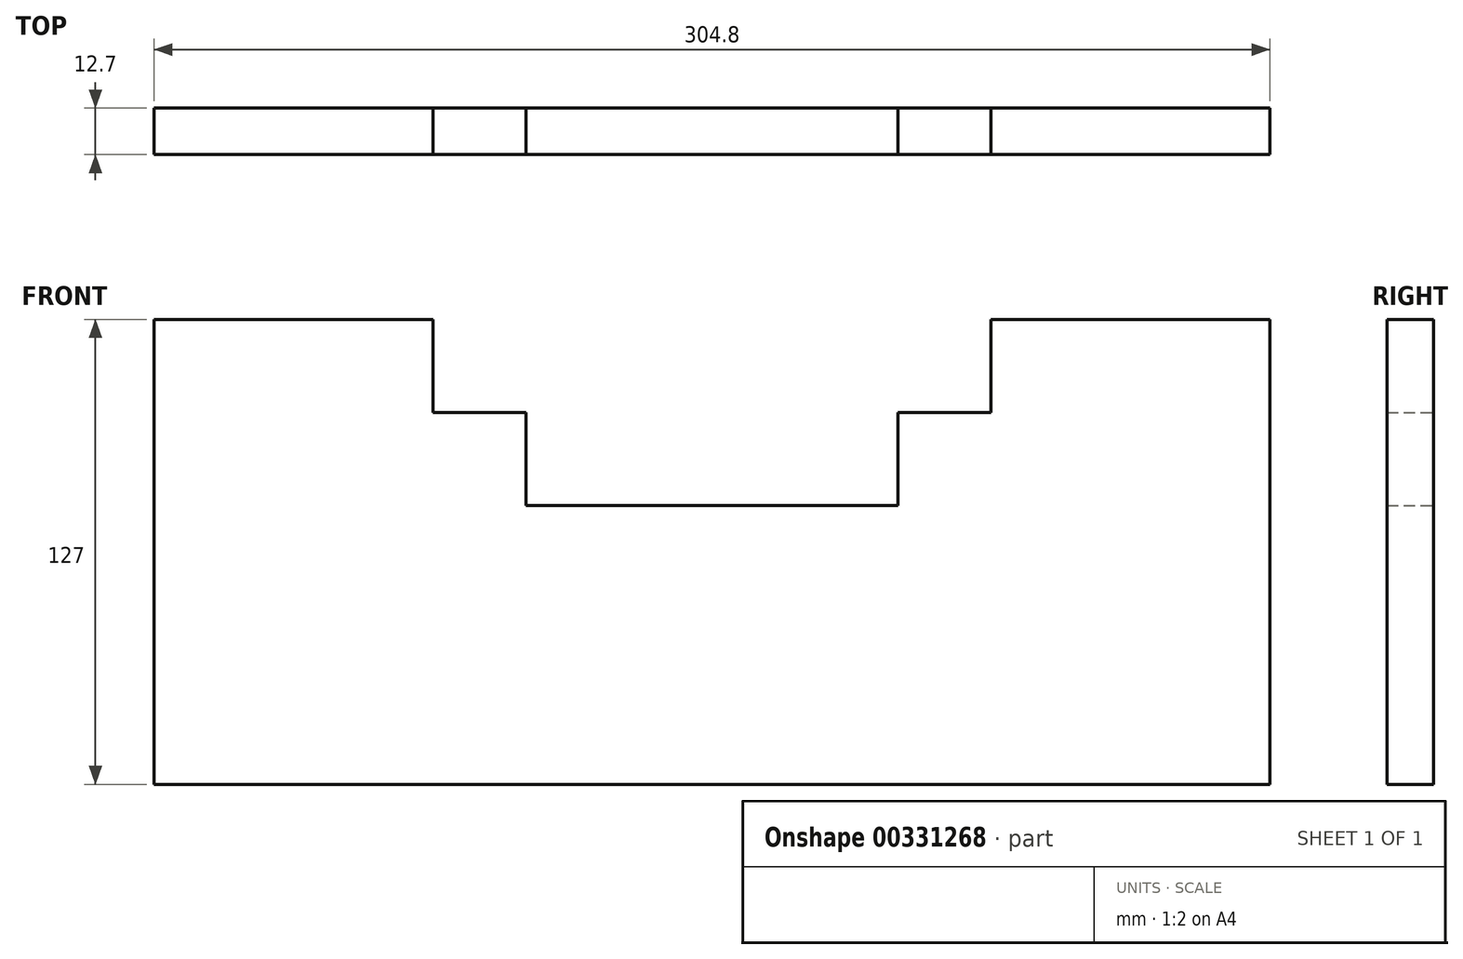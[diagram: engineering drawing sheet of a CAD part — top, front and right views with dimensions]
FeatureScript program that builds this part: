
annotation { "Feature Type Name" : "Feature", "Feature Type Description" : "" }
export const myFeature = defineFeature(function(context is Context, id is Id, definition is map)
    precondition{}
    {
        {
            var Q0;
            Q0=qCreatedBy(makeId("Front.planeOp"),FACE);
            var sketch = newSketch(context, id + "F0", { "sketchPlane" : qUnion([Q0])});
            skLineSegment(sketch, "E0.bottom", {"start": v(-50.8, 76.2) * mm, "end": v(50.8, 76.2) * mm});
            skLineSegment(sketch, "E0.top", {"start": v(-152.4, 0) * mm, "end": v(152.4, 0) * mm});
            skLineSegment(sketch, "E1.bottom", {"start": v(-76.2, 127) * mm, "end": v(-152.4, 127) * mm});
            skLineSegment(sketch, "E1.left", {"start": v(-76.2, 127) * mm, "end": v(-76.2, 101.6) * mm});
            skLineSegment(sketch, "E2.top", {"start": v(152.4, 127) * mm, "end": v(76.2, 127) * mm});
            skLineSegment(sketch, "E2.right", {"start": v(76.2, 101.6) * mm, "end": v(76.2, 127) * mm});
            skLineSegment(sketch, "E3.top", {"start": v(-76.2, 101.6) * mm, "end": v(-50.8, 101.6) * mm});
            skLineSegment(sketch, "E3.right", {"start": v(-50.8, 76.2) * mm, "end": v(-50.8, 101.6) * mm});
            skLineSegment(sketch, "E4.top", {"start": v(76.2, 101.6) * mm, "end": v(50.8, 101.6) * mm});
            skLineSegment(sketch, "E5", {"start": v(50.8, 101.6) * mm, "end": v(50.8, 76.2) * mm});
            skLineSegment(sketch, "E6", {"start": v(-152.4, 127) * mm, "end": v(-152.4, 0) * mm});
            skLineSegment(sketch, "E7", {"start": v(152.4, 127) * mm, "end": v(152.4, 0) * mm});
            skLineSegment(sketch, "E8", {"start": v(0, 76.2) * mm, "end": v(0, 0) * mm, "construction": true});
            skSolve(sketch);
        }
        {
            var Q0;
            Q0 = qSketchRegion(id + "F0", true);
            extrude(context, id + "F1", {"entities" : qUnion([Q0]), "depth" : 12.7 * mm});
        }
    });
